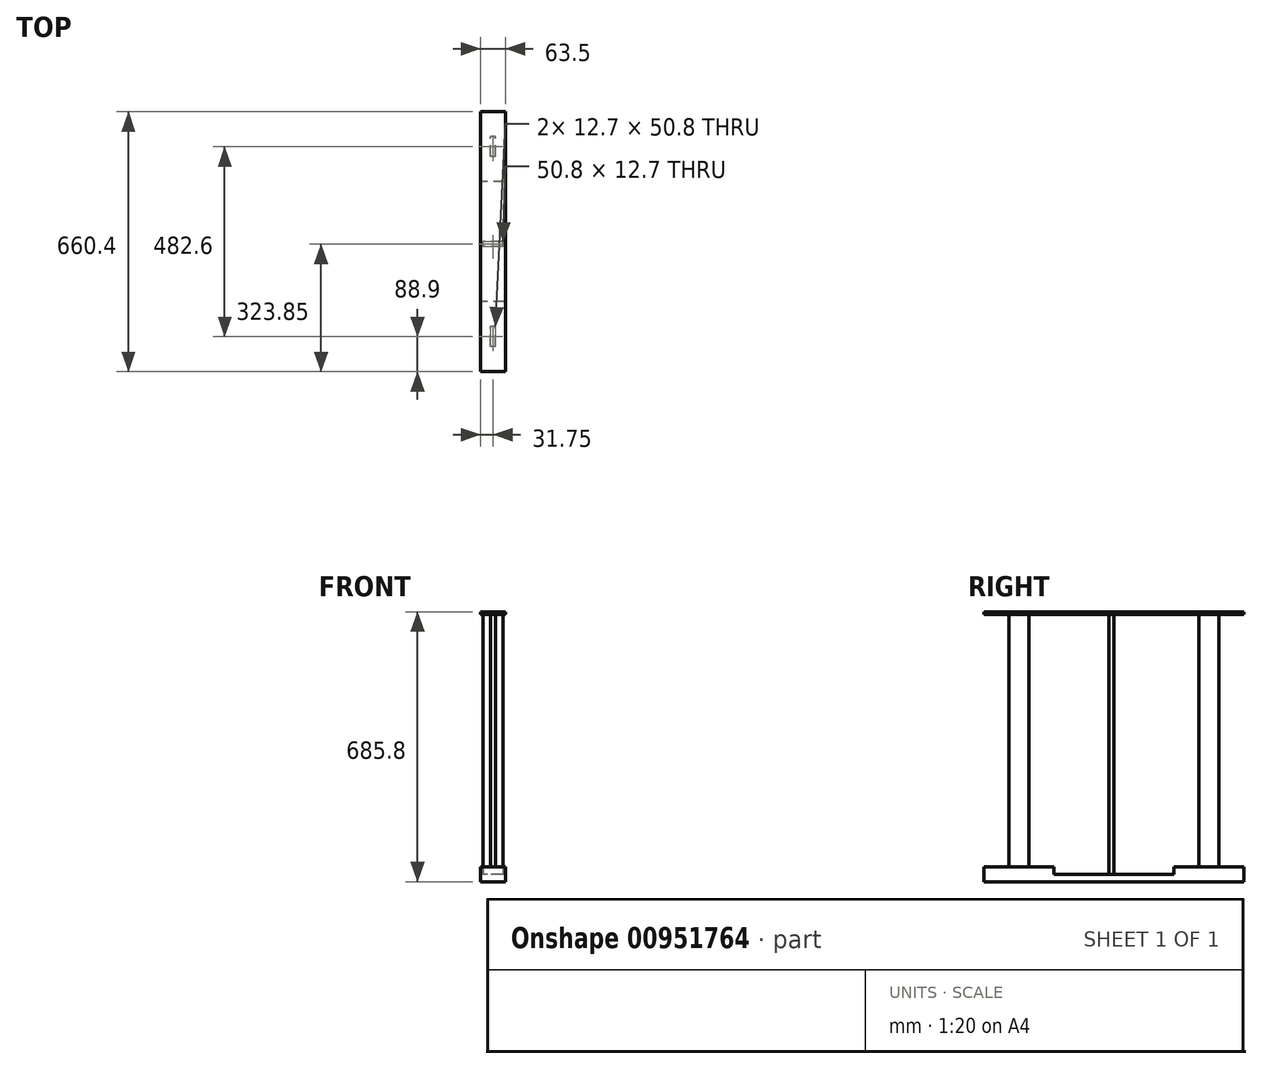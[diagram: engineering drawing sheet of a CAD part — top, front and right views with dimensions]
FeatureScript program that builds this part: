
annotation { "Feature Type Name" : "Feature", "Feature Type Description" : "" }
export const myFeature = defineFeature(function(context is Context, id is Id, definition is map)
    precondition{}
    {
        {
            var Q0;
            Q0=qCreatedBy(makeId("Right.planeOp"),FACE);
            var sketch = newSketch(context, id + "F0", { "sketchPlane" : qUnion([Q0])});
            skLineSegment(sketch, "E0", {"start": v(0, 0) * mm, "end": v(-660.4, 0) * mm});
            skLineSegment(sketch, "E1", {"start": v(0, 38.1) * mm, "end": v(0, 0) * mm});
            skLineSegment(sketch, "E2", {"start": v(0, 38.1) * mm, "end": v(-177.8, 38.1) * mm});
            skLineSegment(sketch, "E3", {"start": v(-177.8, 38.1) * mm, "end": v(-177.8, 19.05) * mm});
            skLineSegment(sketch, "E4", {"start": v(-177.8, 19.05) * mm, "end": v(-482.6, 19.05) * mm});
            skLineSegment(sketch, "E5", {"start": v(-482.6, 19.05) * mm, "end": v(-482.6, 38.1) * mm});
            skLineSegment(sketch, "E6", {"start": v(-482.6, 38.1) * mm, "end": v(-660.4, 38.1) * mm});
            skLineSegment(sketch, "E7", {"start": v(-660.4, 38.1) * mm, "end": v(-660.4, 0) * mm});
            skSolve(sketch);
        }
        {
            var Q0;
            Q0 = qSketchRegion(id + "F0", true);
            extrude(context, id + "F1", {"entities" : qUnion([Q0]), "depth" : 63.5 * mm, "offsetDistance" : 25.4 * mm});
        }
        {
            var Q0;
            Q0=makeQuery(id+"F1.opExtrude","SWEPT_FACE",FACE,{"disambiguationData":[OSD([sQuery(id+"F0.wireOp",EDGE,"E6")])]});
            var sketch = newSketch(context, id + "F2", { "sketchPlane" : qUnion([Q0])});
            skLineSegment(sketch, "E8.bottom", {"start": v(38.1, -596.9) * mm, "end": v(25.4, -596.9) * mm});
            skLineSegment(sketch, "E8.top", {"start": v(38.1, -546.1) * mm, "end": v(25.4, -546.1) * mm});
            skLineSegment(sketch, "E8.left", {"start": v(38.1, -596.9) * mm, "end": v(38.1, -546.1) * mm});
            skLineSegment(sketch, "E8.right", {"start": v(25.4, -596.9) * mm, "end": v(25.4, -546.1) * mm});
            skLineSegment(sketch, "E9.0.1.0", {"start": v(38.1, -114.3) * mm, "end": v(25.4, -114.3) * mm});
            skLineSegment(sketch, "E9.0.1.1", {"start": v(38.1, -63.5) * mm, "end": v(25.4, -63.5) * mm});
            skLineSegment(sketch, "E9.0.1.2", {"start": v(38.1, -114.3) * mm, "end": v(38.1, -63.5) * mm});
            skLineSegment(sketch, "E9.0.1.3", {"start": v(25.4, -114.3) * mm, "end": v(25.4, -63.5) * mm});
            skLineSegment(sketch, "E9.direction1", {"start": v(25.4, -596.9) * mm, "end": v(50.8, -596.9) * mm, "construction": true});
            skLineSegment(sketch, "E9.direction2", {"start": v(25.4, -596.9) * mm, "end": v(25.4, -114.3) * mm, "construction": true});
            skSolve(sketch);
        }
        {
            var Q0;
            Q0=makeQuery(id+"F1.opExtrude","SWEPT_FACE",FACE,{"disambiguationData":[OSD([sQuery(id+"F0.wireOp",EDGE,"E4")])]});
            var sketch = newSketch(context, id + "F3", { "sketchPlane" : qUnion([Q0])});
            skPoint(sketch, "E10.oppositeSnap0", {"position": v(0, -330.2) * mm});
            skLineSegment(sketch, "E10.bottom", {"start": v(57.15, -342.9) * mm, "end": v(6.35, -342.9) * mm});
            skLineSegment(sketch, "E10.top", {"start": v(57.15, -330.2) * mm, "end": v(6.35, -330.2) * mm});
            skLineSegment(sketch, "E10.left", {"start": v(57.15, -342.9) * mm, "end": v(57.15, -330.2) * mm});
            skLineSegment(sketch, "E10.right", {"start": v(6.35, -342.9) * mm, "end": v(6.35, -330.2) * mm});
            skSolve(sketch);
        }
        {
            var Q0;
            Q0 = qSketchRegion(id + "F3", true);
            extrude(context, id + "F4", {"entities" : qUnion([Q0]), "operationType" : NewBodyOperationType.ADD, "depth" : 660.4 * mm, "offsetDistance" : 25.4 * mm});
        }
        {
            var Q0;
            Q0 = qSketchRegion(id + "F2", true);
            extrude(context, id + "F5", {"entities" : qUnion([Q0]), "operationType" : NewBodyOperationType.ADD, "depth" : 641.35 * mm, "offsetDistance" : 25.4 * mm});
        }
        {
            var Q0;
            Q0=makeQuery(id+"F5.opExtrude","CAP_FACE",FACE,{"disambiguationData":[OSD([sQuery(id+"F2.wireOp",EDGE,"E8.bottom"),sQuery(id+"F2.wireOp",EDGE,"E8.top"),sQuery(id+"F2.wireOp",EDGE,"E8.left"),sQuery(id+"F2.wireOp",EDGE,"E8.right")])],"isStart":false});
            var sketch = newSketch(context, id + "F6", { "sketchPlane" : qUnion([Q0])});
            skLineSegment(sketch, "E11.bottom", {"start": v(0, -660.4) * mm, "end": v(63.5, -660.4) * mm});
            skLineSegment(sketch, "E11.top", {"start": v(0, 0) * mm, "end": v(63.5, 0) * mm});
            skLineSegment(sketch, "E11.left", {"start": v(0, -660.4) * mm, "end": v(0, 0) * mm});
            skLineSegment(sketch, "E11.right", {"start": v(63.5, -660.4) * mm, "end": v(63.5, 0) * mm});
            skSolve(sketch);
        }
        {
            var Q0;
            Q0 = qSketchRegion(id + "F6", true);
            extrude(context, id + "F7", {"entities" : qUnion([Q0]), "operationType" : NewBodyOperationType.ADD, "depth" : 6.35 * mm, "offsetDistance" : 25.4 * mm});
        }
    });
